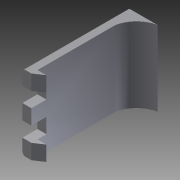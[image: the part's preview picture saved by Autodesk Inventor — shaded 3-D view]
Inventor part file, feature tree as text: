
AUTODESK INVENTOR PART (.ipt)
format: ipt  version: 2012 (Build 160160000, 160)  size: 112,128 bytes
history: native  units: mm
features: extrude x3, sketch x3, fillet x2
ambient origin geometry x8: Origin, YZ Plane, XZ Plane, XY Plane, X Axis, Y Axis, Z Axis, Center Point
bodies: Solid1 (feature_tree)
feature tree (8):
  extrude  "Extrusion1"  Depth=3.0mm
  fillet  "Fillet1"  Radius=7.0mm
  fillet  "Fillet2"  Radius=7.0mm
  extrude  "Extrusion2"  Depth=1.0mm
  extrude  "Extrusion3"  Depth=5.0mm
  sketch  "Sketch1"  dims[d7=9.0mm d8=3.0mm d9=7.0mm d10=7.0mm]
  sketch  "Sketch2"  dims[d11=25.0mm d12=0.0mm d13=1.0mm]
  sketch  "Sketch3"  dims[d14=1.0mm d17=5.0mm d20=5.0mm d21=0.0mm d22=5.0mm d23=0.0mm]
